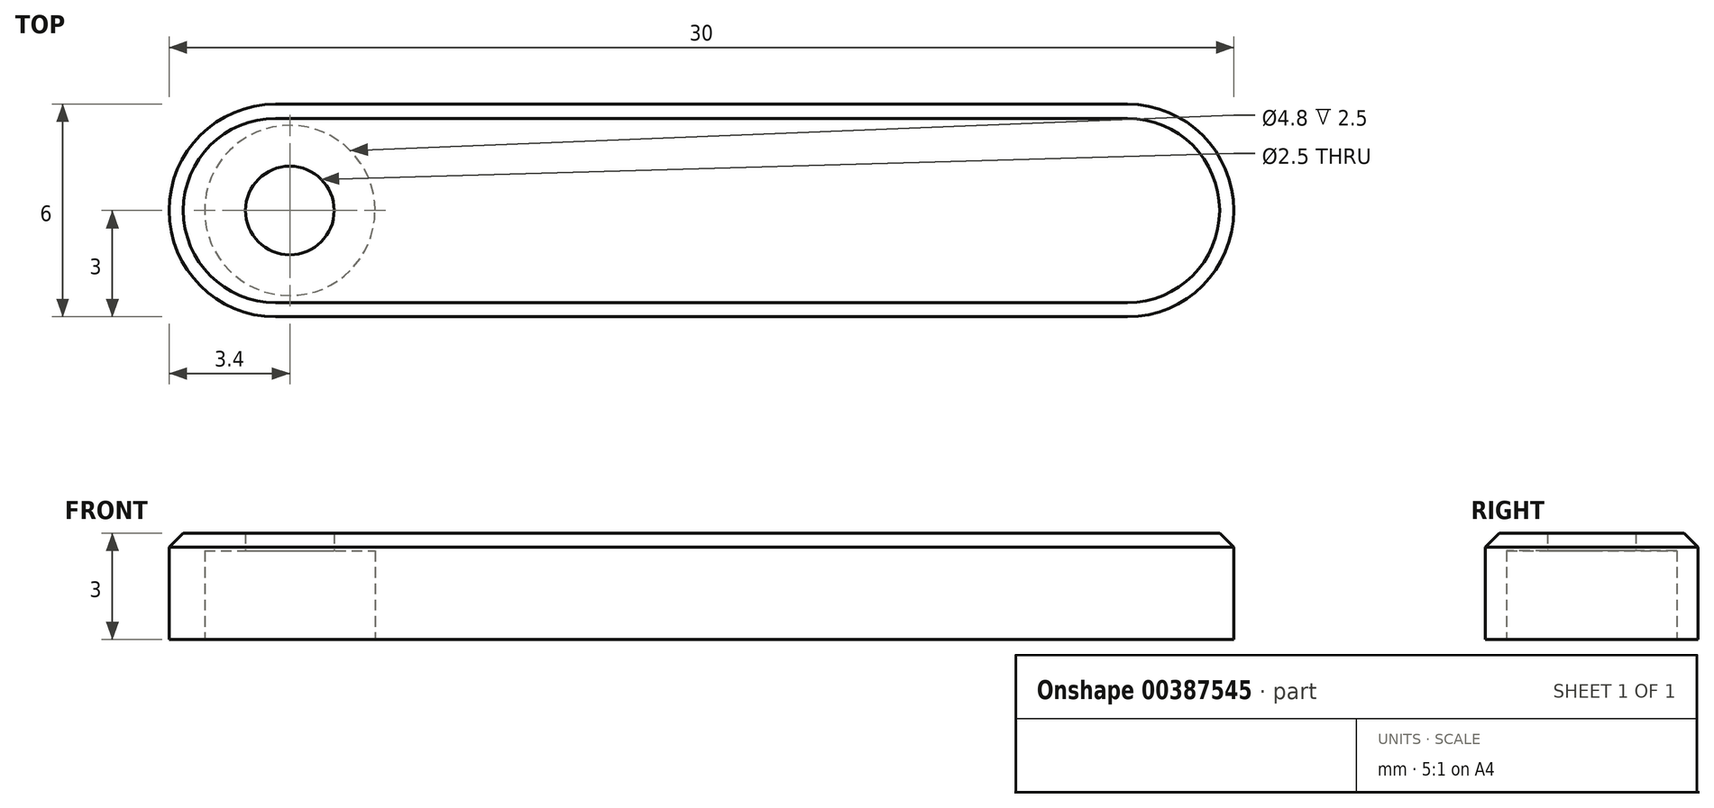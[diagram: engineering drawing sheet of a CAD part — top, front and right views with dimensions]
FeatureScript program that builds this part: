
annotation { "Feature Type Name" : "Feature", "Feature Type Description" : "" }
export const myFeature = defineFeature(function(context is Context, id is Id, definition is map)
    precondition{}
    {
        {
            var Q0;
            Q0=qCreatedBy(makeId("Top.planeOp"),FACE);
            var sketch = newSketch(context, id + "F0", { "sketchPlane" : qUnion([Q0])});
            skLineSegment(sketch, "E0.bottom", {"start": v(0, 3) * mm, "end": v(30, 3) * mm});
            skLineSegment(sketch, "E0.top", {"start": v(0, -3) * mm, "end": v(30, -3) * mm});
            skLineSegment(sketch, "E0.left", {"start": v(0, 3) * mm, "end": v(0, -3) * mm});
            skLineSegment(sketch, "E0.right", {"start": v(30, 3) * mm, "end": v(30, -3) * mm});
            skSolve(sketch);
        }
        {
            var Q0;
            Q0=qSketchRegion(id+"F0",true);
            extrude(context, id + "F1", {"entities" : qUnion([Q0]), "depth" : 3 * mm});
        }
        {
            var Q0;
            Q0=makeQuery(id+"F1.opExtrude","CAP_FACE",FACE,{"disambiguationData":[OSD([sQuery(id+"F0.wireOp",EDGE,"E0.bottom"),sQuery(id+"F0.wireOp",EDGE,"E0.top"),sQuery(id+"F0.wireOp",EDGE,"E0.left"),sQuery(id+"F0.wireOp",EDGE,"E0.right")])],"isStart":true});
            var sketch = newSketch(context, id + "F2", { "sketchPlane" : qUnion([Q0])});
            skCircle(sketch, "E1", {"center": v(3.4, 0) * mm, "radius": 2.4 * mm});
            skPoint(sketch, "E1.centerSnap0", {"position": v(0, 0) * mm});
            skCircle(sketch, "E2", {"center": v(3.4, 0) * mm, "radius": 1.25 * mm});
            skSolve(sketch);
        }
        {
            var Q0;
            Q0=makeQuery(id+"F2.imprint","IMPRINT",FACE,{"disambiguationData":[TD([[makeQuery(id+"F2.imprint","IMPRINT",EDGE,{"derivedFrom":sQuery(id+"F2.wireOp",EDGE,"E1")}),1.0]])]});
            var Q1;
            Q1=makeQuery(id+"F2.imprint","IMPRINT",FACE,{"disambiguationData":[TD([[makeQuery(id+"F2.imprint","IMPRINT",EDGE,{"derivedFrom":sQuery(id+"F2.wireOp",EDGE,"E2")}),1.0]])]});
            extrude(context, id + "F3", {"entities" : qUnion([Q0, Q1]), "operationType" : NewBodyOperationType.REMOVE, "oppositeDirection" : true, "depth" : 2.5 * mm});
        }
        {
            var Q0;
            Q0=makeQuery(id+"F2.imprint","IMPRINT",FACE,{"disambiguationData":[TD([[makeQuery(id+"F2.imprint","IMPRINT",EDGE,{"derivedFrom":sQuery(id+"F2.wireOp",EDGE,"E2")}),1.0]])]});
            extrude(context, id + "F4", {"entities" : qUnion([Q0]), "operationType" : NewBodyOperationType.REMOVE, "endBound" : BoundingType.THROUGH_ALL, "oppositeDirection" : true, "depth" : 25 * mm});
        }
        {
            var Q0;
            Q0=makeQuery(id+"F1.opExtrude","SWEPT_EDGE",EDGE,{"disambiguationData":[OSD([sQuery(id+"F0.wireOp",EDGE,"E0.top"),sQuery(id+"F0.wireOp",EDGE,"E0.left")])]});
            var Q1;
            Q1=makeQuery(id+"F1.opExtrude","SWEPT_EDGE",EDGE,{"disambiguationData":[OSD([sQuery(id+"F0.wireOp",EDGE,"E0.bottom"),sQuery(id+"F0.wireOp",EDGE,"E0.left")])]});
            var Q2;
            Q2=makeQuery(id+"F1.opExtrude","SWEPT_EDGE",EDGE,{"disambiguationData":[OSD([sQuery(id+"F0.wireOp",EDGE,"E0.top"),sQuery(id+"F0.wireOp",EDGE,"E0.right")])]});
            var Q3;
            Q3=makeQuery(id+"F1.opExtrude","SWEPT_EDGE",EDGE,{"disambiguationData":[OSD([sQuery(id+"F0.wireOp",EDGE,"E0.bottom"),sQuery(id+"F0.wireOp",EDGE,"E0.right")])]});
            fillet(context, id + "F5", {"entities" : qUnion([Q0, Q1, Q2, Q3]), "radius" : 3 * mm, "tangentPropagation" : true, "allowEdgeOverflow" : false});
        }
        {
            var Q0;
            Q0=makeQuery(id+"F1.opExtrude","CAP_EDGE",EDGE,{"disambiguationData":[OSD([sQuery(id+"F0.wireOp",EDGE,"E0.bottom")])],"isStart":false});
            chamfer(context, id + "F6", {"entities" : qUnion([Q0]), "width" : 0.4 * mm, "tangentPropagation" : true});
        }
    });
